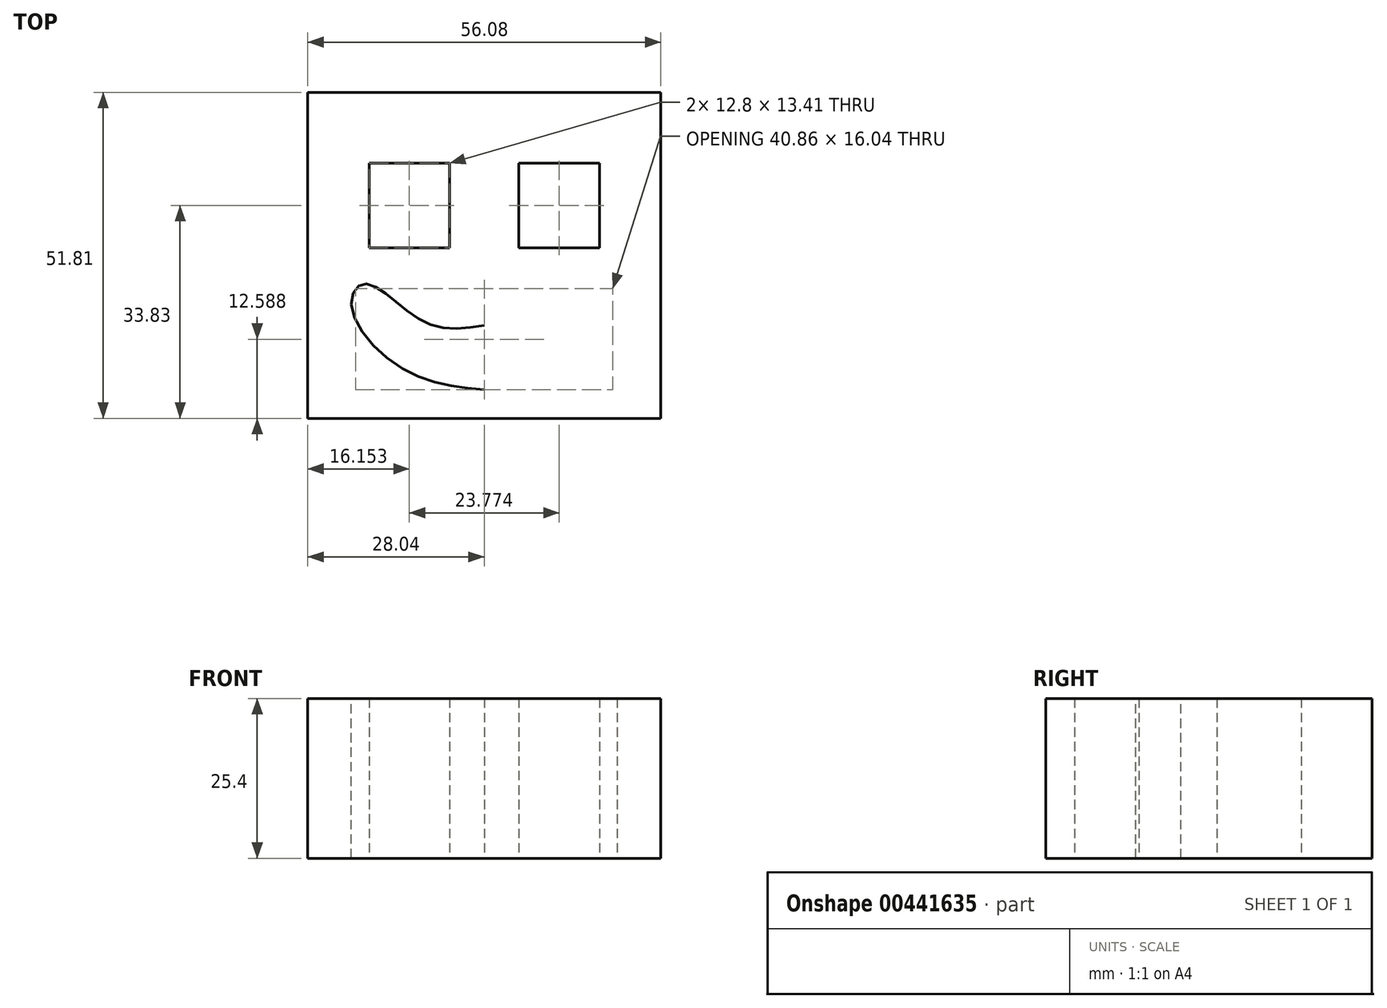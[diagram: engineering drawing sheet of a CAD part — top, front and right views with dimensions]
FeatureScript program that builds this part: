
annotation { "Feature Type Name" : "Feature", "Feature Type Description" : "" }
export const myFeature = defineFeature(function(context is Context, id is Id, definition is map)
    precondition{}
    {
        {
            var Q0;
            Q0=qCreatedBy(makeId("Top.planeOp"),FACE);
            var sketch = newSketch(context, id + "F0", { "sketchPlane" : qUnion([Q0])});
            skLineSegment(sketch, "E0", {"start": v(0, 37.03) * mm, "end": v(-28.04, 37.03) * mm});
            skLineSegment(sketch, "E1", {"start": v(-28.04, 37.03) * mm, "end": v(-28.04, -14.78) * mm});
            skLineSegment(sketch, "E2", {"start": v(-28.04, -14.78) * mm, "end": v(-5.18, -14.78) * mm});
            skLineSegment(sketch, "E3", {"start": v(-5.18, -14.78) * mm, "end": v(-28.04, -14.78) * mm});
            skLineSegment(sketch, "E4.MirrorCS", {"start": v(28.04, -14.78) * mm, "end": v(0, -14.78) * mm});
            skLineSegment(sketch, "E5.MirrorCS", {"start": v(5.18, -14.78) * mm, "end": v(28.04, -14.78) * mm});
            skLineSegment(sketch, "E6.MirrorCS", {"start": v(0, 37.03) * mm, "end": v(28.04, 37.03) * mm});
            skLineSegment(sketch, "E7.MirrorCS", {"start": v(28.04, 37.03) * mm, "end": v(28.04, -14.78) * mm});
            skLineSegment(sketch, "E8.bottom", {"start": v(-18.29, 25.76) * mm, "end": v(-5.49, 25.76) * mm});
            skLineSegment(sketch, "E8.top", {"start": v(-18.29, 12.34) * mm, "end": v(-5.49, 12.34) * mm});
            skLineSegment(sketch, "E8.left", {"start": v(-18.29, 25.76) * mm, "end": v(-18.29, 12.34) * mm});
            skLineSegment(sketch, "E8.right", {"start": v(-5.49, 25.76) * mm, "end": v(-5.49, 12.34) * mm});
            skLineSegment(sketch, "E9.MirrorCS", {"start": v(5.49, 25.76) * mm, "end": v(5.49, 12.34) * mm});
            skLineSegment(sketch, "E10.MirrorCS", {"start": v(18.29, 25.76) * mm, "end": v(5.49, 25.76) * mm});
            skLineSegment(sketch, "E11.MirrorCS", {"start": v(18.29, 12.34) * mm, "end": v(5.49, 12.34) * mm});
            skLineSegment(sketch, "E12.MirrorCS", {"start": v(18.29, 25.76) * mm, "end": v(18.29, 12.34) * mm});
            skFitSpline(sketch, "E13", {"points": [v(0, 0) * mm, v(-8.23, 0) * mm, v(-15.24, 4.72) * mm, v(-19.5, 6.55) * mm, v(-21.03, 2.6) * mm, v(-12.5, -7.16) * mm, v(0, -10.21) * mm], "startDerivative": vector(-51.04, -7.64) * mm, "endDerivative": vector(60.68, -5.69) * mm});
            skFitSpline(sketch, "E14.MirrorCS", {"points": [v(0, 0) * mm, v(8.23, 0) * mm, v(15.24, 4.72) * mm, v(19.5, 6.55) * mm, v(21.03, 2.6) * mm, v(12.5, -7.16) * mm, v(0, -10.21) * mm], "startDerivative": vector(51.04, -7.64) * mm, "endDerivative": vector(-60.68, -5.69) * mm});
            skPoint(sketch, "E15.orphan", {"position": v(0, -14.78) * mm});
            skPoint(sketch, "E16.MirrorCS.start.orphan", {"position": v(0, -26.06) * mm});
            skPoint(sketch, "E17.top.start.orphan", {"position": v(-5.18, -31.85) * mm});
            skLineSegment(sketch, "E18", {"start": v(0, -14.78) * mm, "end": v(-5.18, -14.78) * mm});
            skPoint(sketch, "E19.bottom.end.orphan", {"position": v(-5.18, -26.06) * mm});
            skPoint(sketch, "E19.left.start.orphan", {"position": v(-12.5, -26.06) * mm});
            skPoint(sketch, "E19.top.end.orphan", {"position": v(0, -31.85) * mm});
            skPoint(sketch, "E20.orphan", {"position": v(-12.5, -31.85) * mm});
            skPoint(sketch, "E21.MirrorCS.end.orphan", {"position": v(5.18, -26.06) * mm});
            skPoint(sketch, "E22.MirrorCS.start.orphan", {"position": v(12.5, -26.06) * mm});
            skPoint(sketch, "E23.MirrorCS.end.orphan", {"position": v(5.18, -31.85) * mm});
            skPoint(sketch, "E23.MirrorCS.start.orphan", {"position": v(12.5, -31.85) * mm});
            skPoint(sketch, "E24.orphan", {"position": v(0, 50.75) * mm});
            skSolve(sketch);
        }
        {
            var Q0;
            Q0=makeQuery(id+"F0.imprint","IMPRINT",FACE,{"disambiguationData":[TD([[makeQuery(id+"F0.imprint","IMPRINT",EDGE,{"derivedFrom":sQuery(id+"F0.wireOp",EDGE,"E0")}),1.0]])]});
            extrude(context, id + "F1", {"entities" : qUnion([Q0]), "depth" : 25.4 * mm});
        }
    });
